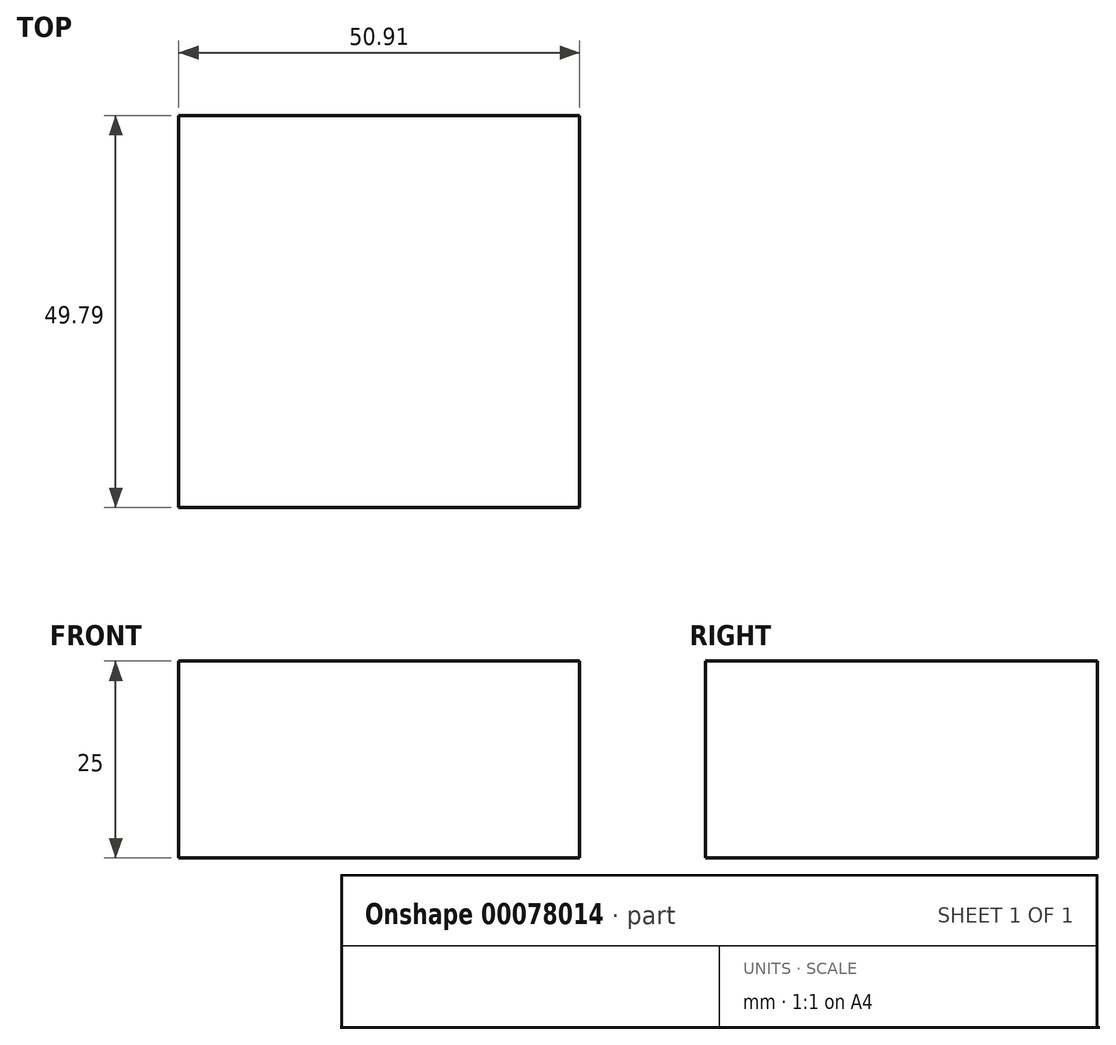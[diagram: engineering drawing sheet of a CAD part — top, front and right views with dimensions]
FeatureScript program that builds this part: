
annotation { "Feature Type Name" : "Feature", "Feature Type Description" : "" }
export const myFeature = defineFeature(function(context is Context, id is Id, definition is map)
    precondition{}
    {
        {
            var Q0;
            Q0=qCreatedBy(makeId("Top.planeOp"),FACE);
            var sketch = newSketch(context, id + "F0", { "sketchPlane" : qUnion([Q0])});
            skLineSegment(sketch, "E0.bottom", {"start": v(-26.37, -4.3) * mm, "end": v(24.54, -4.3) * mm});
            skLineSegment(sketch, "E0.top", {"start": v(-26.37, 45.5) * mm, "end": v(24.54, 45.5) * mm});
            skLineSegment(sketch, "E0.left", {"start": v(-26.37, -4.3) * mm, "end": v(-26.37, 45.5) * mm});
            skLineSegment(sketch, "E0.right", {"start": v(24.54, -4.3) * mm, "end": v(24.54, 45.5) * mm});
            skSolve(sketch);
        }
        {
            var Q0;
            Q0=makeQuery(id+"F0.imprint","IMPRINT",FACE,{"disambiguationData":[TD([[makeQuery(id+"F0.imprint","IMPRINT",EDGE,{"derivedFrom":sQuery(id+"F0.wireOp",EDGE,"E0.bottom")}),1.0]])]});
            extrude(context, id + "F1", {"entities" : qUnion([Q0]), "depth" : 25 * mm});
        }
    });
